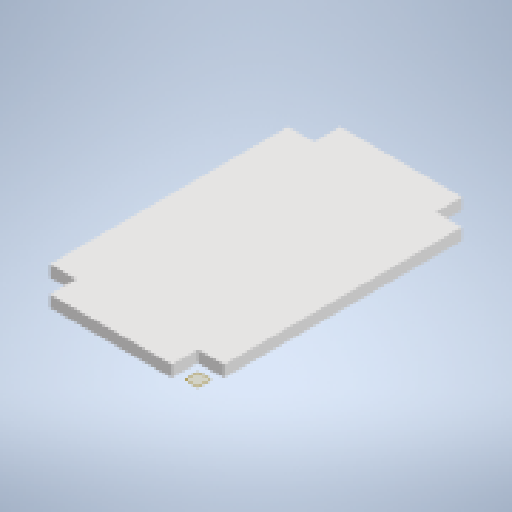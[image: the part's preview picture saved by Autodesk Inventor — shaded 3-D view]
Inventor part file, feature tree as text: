
AUTODESK INVENTOR PART (.ipt)
format: ipt  version: 2024 (Build 280153000, 153)  size: 145,920 bytes
history: native  units: mm
features: sketch x1, plane x1, extrude x1
ambient origin geometry x8: Origin, YZ Plane, XZ Plane, XY Plane, X Axis, Y Axis, Z Axis, Center Point
bodies: Body1 (feature_tree)
feature tree (3):
  sketch  "Sketch2"  dims[d0=300.0mm d1=500.0mm d12=45.0mm d13=45.0mm d14=45.0mm d15=45.0mm d16=45.0mm d17=45.0mm d18=45.0mm d19=45.0mm d20=20.0mm d21=0.0mm]
  plane  "Work Plane1"
  extrude  "Extrusion2"  Depth=500.0mm
